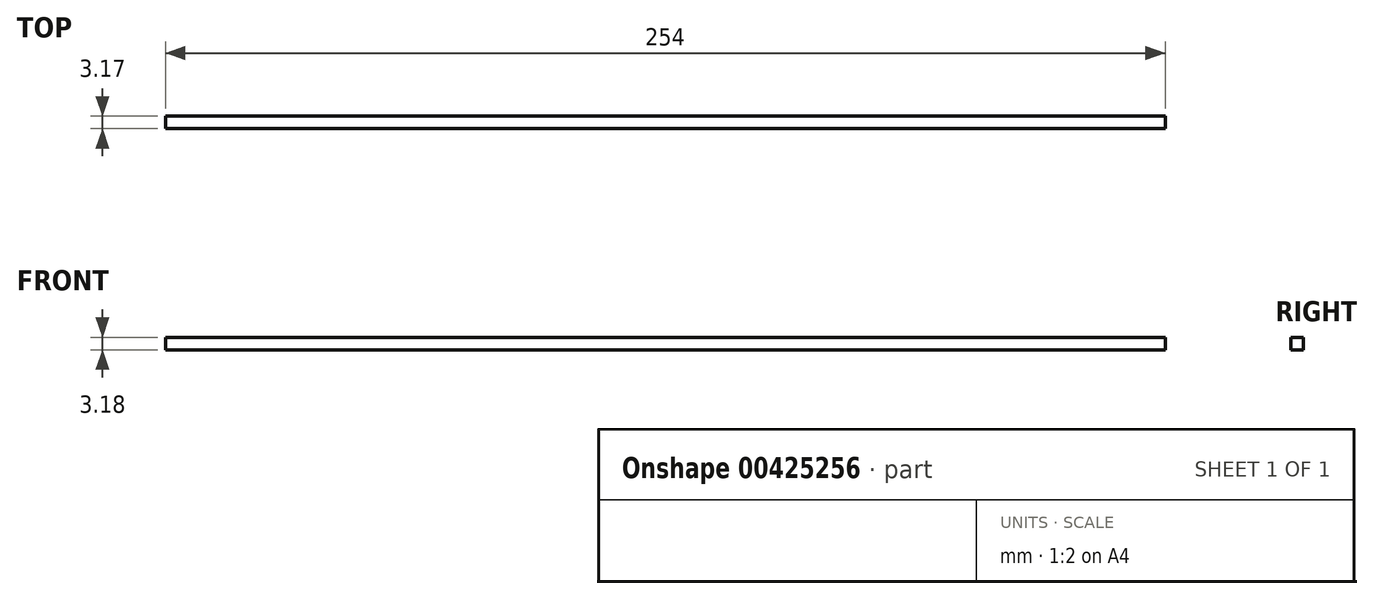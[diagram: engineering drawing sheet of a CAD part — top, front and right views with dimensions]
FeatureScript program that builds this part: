
annotation { "Feature Type Name" : "Feature", "Feature Type Description" : "" }
export const myFeature = defineFeature(function(context is Context, id is Id, definition is map)
    precondition{}
    {
        {
            var Q0;
            Q0=qCreatedBy(makeId("Front.planeOp"),FACE);
            var sketch = newSketch(context, id + "F0", { "sketchPlane" : qUnion([Q0])});
            skLineSegment(sketch, "E0.bottom", {"start": v(-41.53, 31.23) * mm, "end": v(212.47, 31.23) * mm});
            skLineSegment(sketch, "E0.top", {"start": v(-41.53, 28.05) * mm, "end": v(212.47, 28.05) * mm});
            skLineSegment(sketch, "E0.left", {"start": v(-41.53, 31.23) * mm, "end": v(-41.53, 28.05) * mm});
            skLineSegment(sketch, "E0.right", {"start": v(212.47, 31.23) * mm, "end": v(212.47, 28.05) * mm});
            skSolve(sketch);
        }
        {
            var Q0;
            Q0 = qSketchRegion(id + "F0", true);
            extrude(context, id + "F1", {"entities" : qUnion([Q0]), "depth" : 3.17 * mm});
        }
    });
